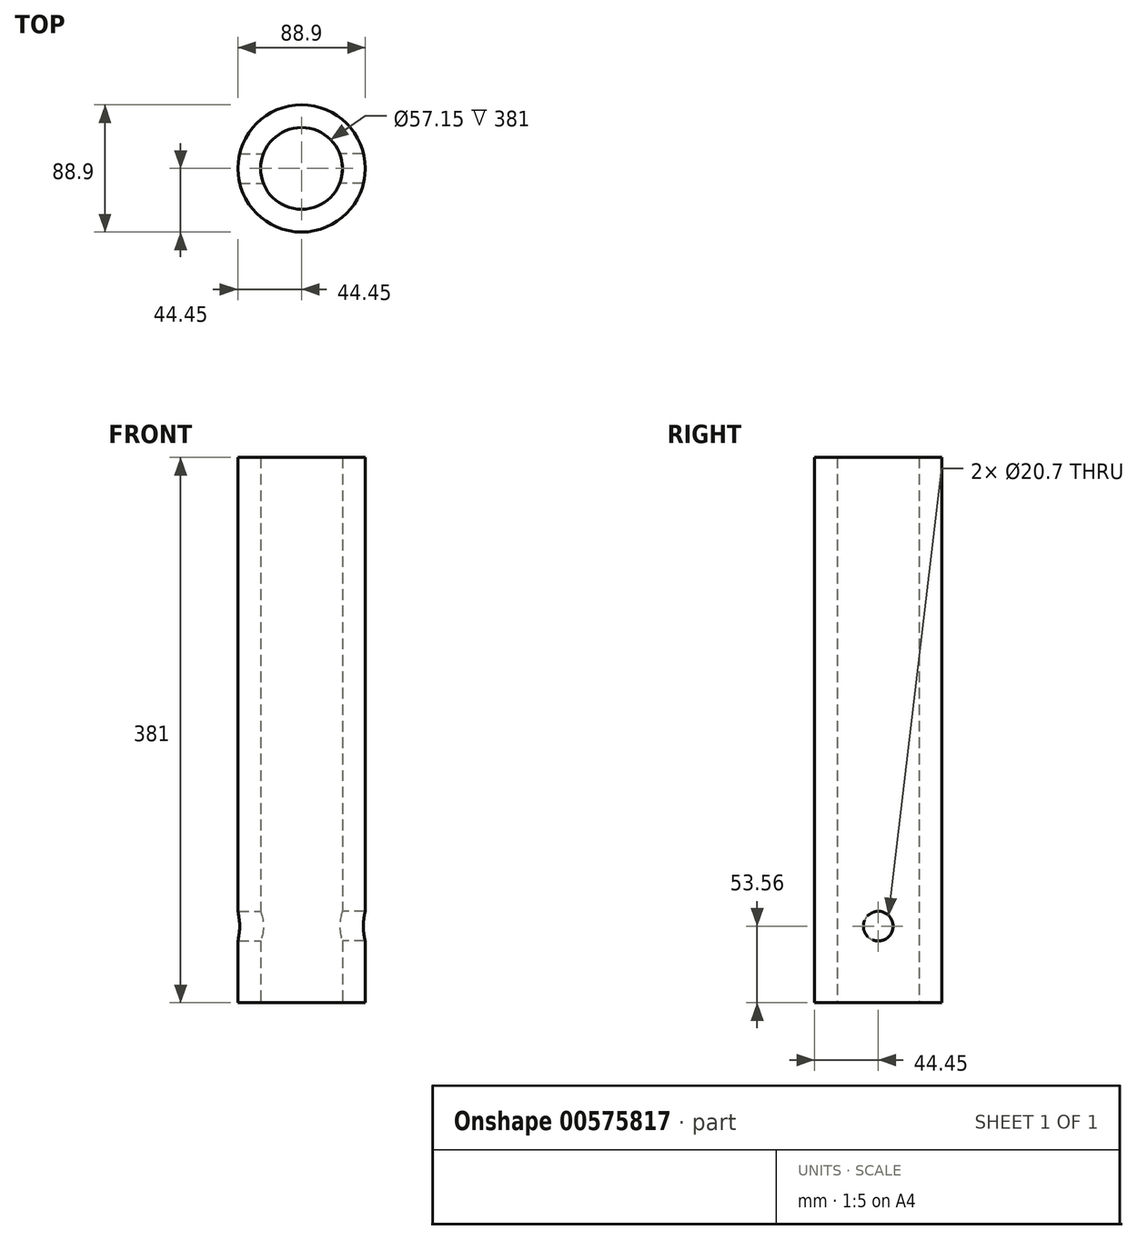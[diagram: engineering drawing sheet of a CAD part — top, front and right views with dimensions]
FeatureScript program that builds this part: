
annotation { "Feature Type Name" : "Feature", "Feature Type Description" : "" }
export const myFeature = defineFeature(function(context is Context, id is Id, definition is map)
    precondition{}
    {
        {
            var Q0;
            Q0=qCreatedBy(makeId("Top.planeOp"),FACE);
            var sketch = newSketch(context, id + "F0", { "sketchPlane" : qUnion([Q0])});
            skCircle(sketch, "E0", {"center": v(0, 0) * mm, "radius": 44.45 * mm});
            skCircle(sketch, "E1", {"center": v(0, 0) * mm, "radius": 28.58 * mm});
            skSolve(sketch);
        }
        {
            var Q0;
            Q0=makeQuery(id+"F0.imprint","IMPRINT",FACE,{"disambiguationData":[TD([[makeQuery(id+"F0.imprint","IMPRINT",EDGE,{"derivedFrom":sQuery(id+"F0.wireOp",EDGE,"E0")}),1.0]])]});
            extrude(context, id + "F1", {"entities" : qUnion([Q0]), "depth" : 381 * mm, "offsetDistance" : 25.4 * mm});
        }
        {
            var Q0;
            Q0=qCreatedBy(makeId("Right.planeOp"),FACE);
            var sketch = newSketch(context, id + "F2", { "sketchPlane" : qUnion([Q0])});
            skCircle(sketch, "E2", {"center": v(0, 53.56) * mm, "radius": 10.35 * mm});
            skSolve(sketch);
        }
        {
            var Q0;
            Q0 = qSketchRegion(id + "F2", true);
            extrude(context, id + "F3", {"entities" : qUnion([Q0]), "operationType" : NewBodyOperationType.REMOVE, "oppositeDirection" : true, "depth" : 119.89 * mm, "offsetDistance" : 25.4 * mm});
        }
        {
            var Q0;
            Q0 = qSketchRegion(id + "F2", true);
            extrude(context, id + "F4", {"entities" : qUnion([Q0]), "operationType" : NewBodyOperationType.REMOVE, "depth" : 65.8 * mm, "offsetDistance" : 25.4 * mm});
        }
    });
